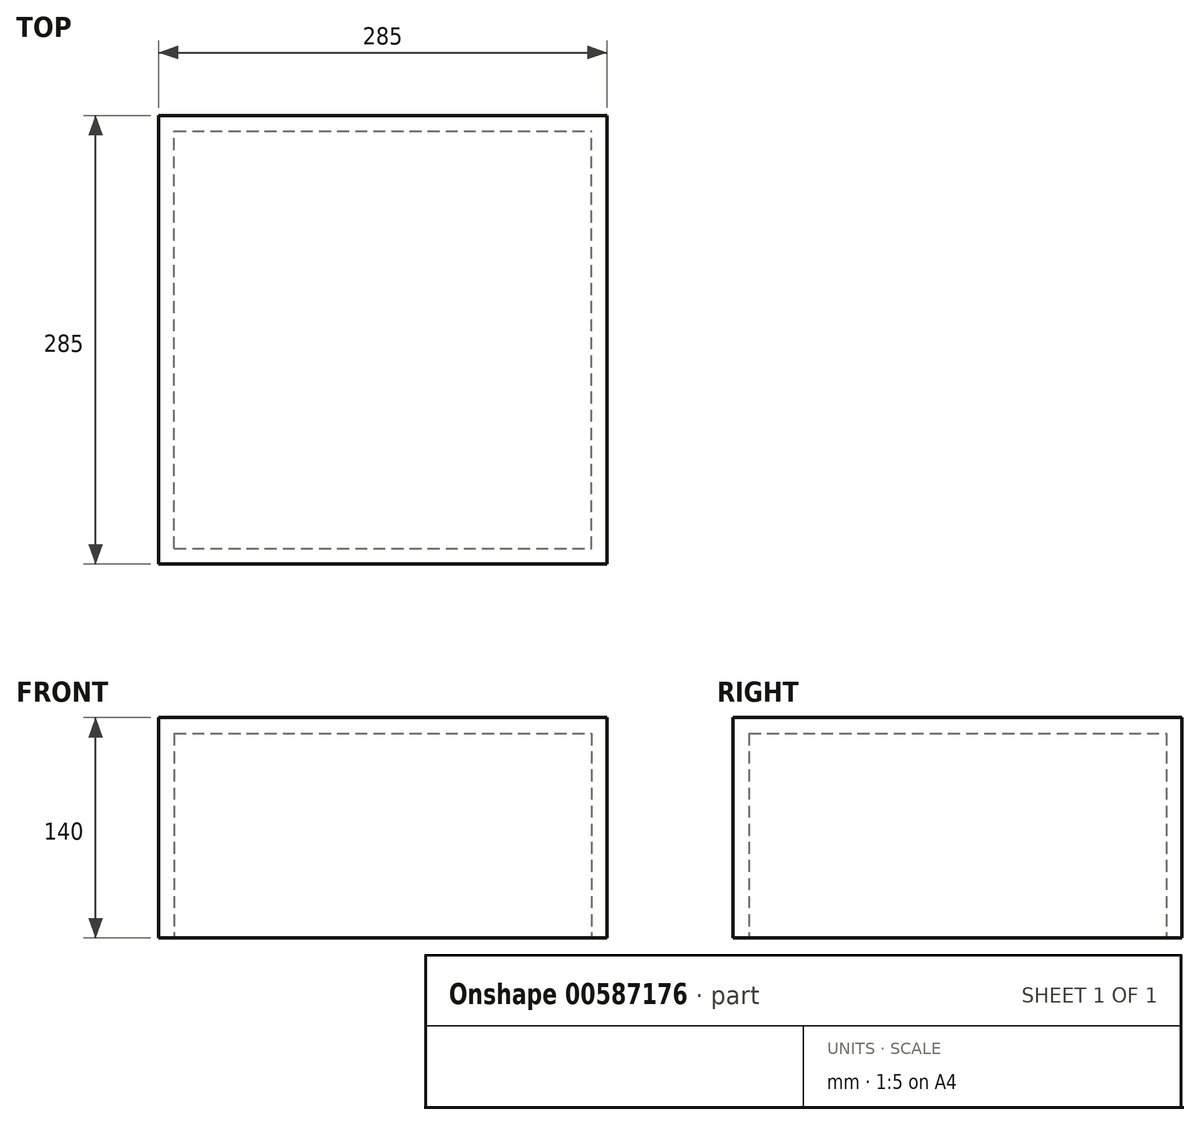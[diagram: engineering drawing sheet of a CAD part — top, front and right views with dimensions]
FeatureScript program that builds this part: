
annotation { "Feature Type Name" : "Feature", "Feature Type Description" : "" }
export const myFeature = defineFeature(function(context is Context, id is Id, definition is map)
    precondition{}
    {
        {
            var Q0;
            Q0=qCreatedBy(makeId("Top.planeOp"),FACE);
            var sketch = newSketch(context, id + "F0", { "sketchPlane" : qUnion([Q0])});
            skLineSegment(sketch, "E0.bottom", {"start": v(-142.5, -142.5) * mm, "end": v(142.5, -142.5) * mm});
            skLineSegment(sketch, "E0.top", {"start": v(-142.5, 142.5) * mm, "end": v(142.5, 142.5) * mm});
            skLineSegment(sketch, "E0.left", {"start": v(-142.5, -142.5) * mm, "end": v(-142.5, 142.5) * mm});
            skLineSegment(sketch, "E0.right", {"start": v(142.5, -142.5) * mm, "end": v(142.5, 142.5) * mm});
            skPoint(sketch, "E0.middle", {"position": v(0, 0) * mm});
            skSolve(sketch);
        }
        {
            var Q0;
            Q0 = qSketchRegion(id + "F0", true);
            extrude(context, id + "F1", {"entities" : qUnion([Q0]), "endBound" : BoundingType.SYMMETRIC, "depth" : 140 * mm, "offsetDistance" : 25.4 * mm});
        }
        {
            var Q0;
            Q0=makeQuery(id+"F1.opExtrude","CAP_FACE",FACE,{"disambiguationData":[OSD([sQuery(id+"F0.wireOp",EDGE,"E0.bottom"),sQuery(id+"F0.wireOp",EDGE,"E0.top"),sQuery(id+"F0.wireOp",EDGE,"E0.left"),sQuery(id+"F0.wireOp",EDGE,"E0.right")])],"isStart":true});
            shell(context, id + "F2", {"entities" : qUnion([Q0]), "thickness" : 10 * mm});
        }
    });
